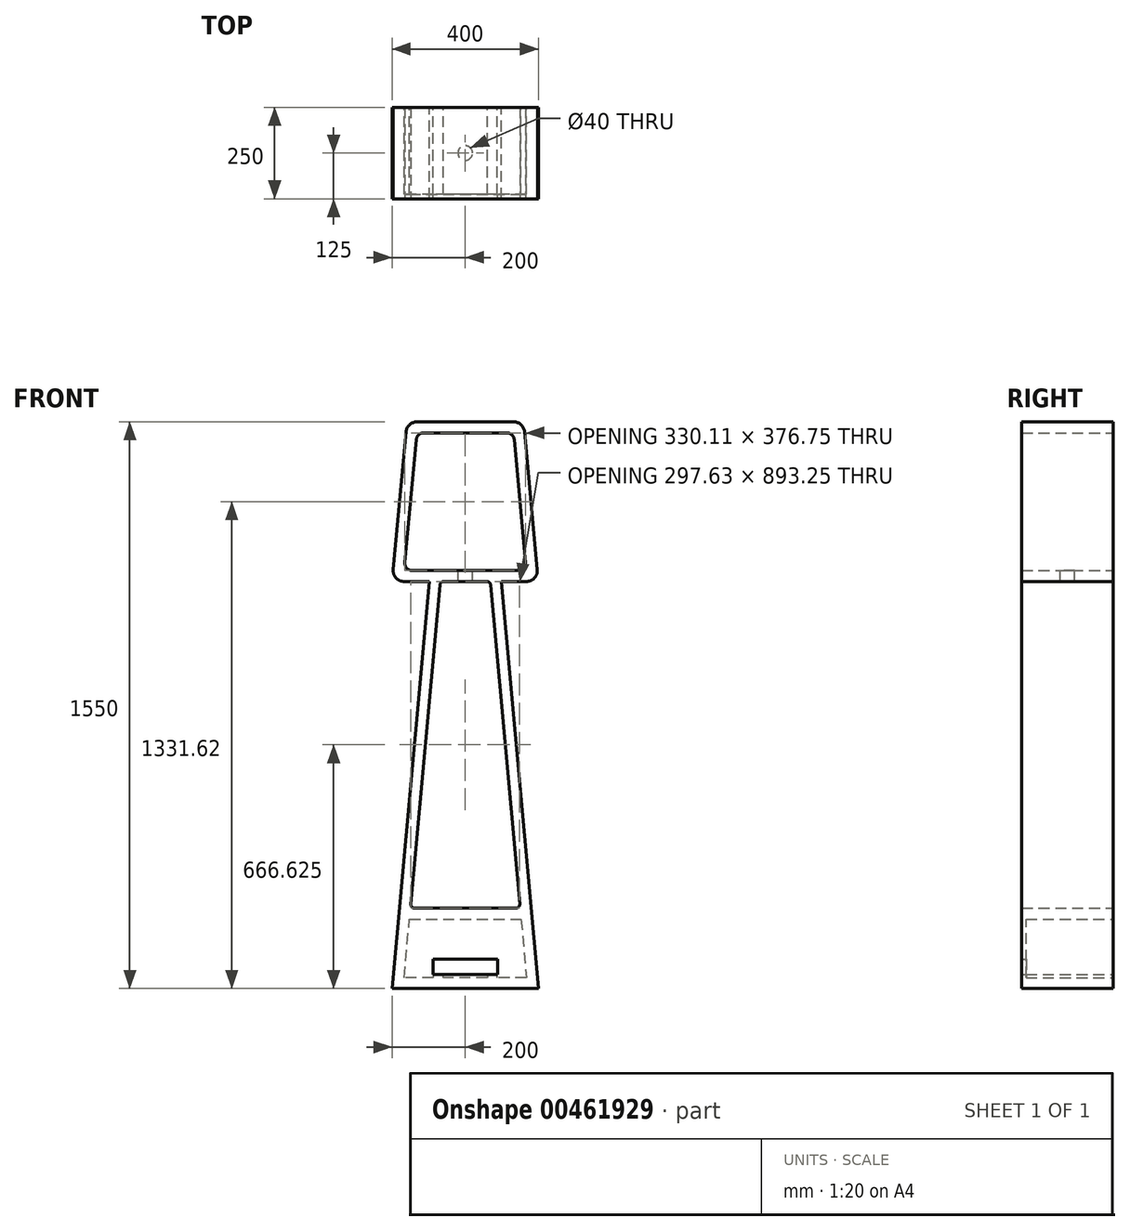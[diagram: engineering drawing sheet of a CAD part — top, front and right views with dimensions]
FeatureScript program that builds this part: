
annotation { "Feature Type Name" : "Feature", "Feature Type Description" : "" }
export const myFeature = defineFeature(function(context is Context, id is Id, definition is map)
    precondition{}
    {
        {
            var Q0;
            Q0=qCreatedBy(makeId("Front.planeOp"),FACE);
            var sketch = newSketch(context, id + "F0", { "sketchPlane" : qUnion([Q0])});
            skLineSegment(sketch, "E0", {"start": v(98.47, 1113.25) * mm, "end": v(200, 1113.25) * mm});
            skLineSegment(sketch, "E1", {"start": v(200, 1113.25) * mm, "end": v(159.42, 1550) * mm});
            skLineSegment(sketch, "E2.MirrorCS", {"start": v(-200, 1113.25) * mm, "end": v(-159.42, 1550) * mm});
            skLineSegment(sketch, "E3.MirrorCS", {"start": v(-98.47, 1113.25) * mm, "end": v(-200, 1113.25) * mm});
            skLineSegment(sketch, "E4", {"start": v(-159.42, 1550) * mm, "end": v(159.42, 1550) * mm});
            skLineSegment(sketch, "E5", {"start": v(200, 0) * mm, "end": v(-200, 0) * mm});
            skLineSegment(sketch, "E6", {"start": v(-132.08, 1520) * mm, "end": v(-167.08, 1143.25) * mm});
            skLineSegment(sketch, "E7", {"start": v(-167.08, 1143.25) * mm, "end": v(167.08, 1143.25) * mm});
            skLineSegment(sketch, "E8", {"start": v(167.08, 1143.25) * mm, "end": v(132.08, 1520) * mm});
            skLineSegment(sketch, "E9", {"start": v(132.08, 1520) * mm, "end": v(-132.08, 1520) * mm});
            skLineSegment(sketch, "E10", {"start": v(-98.47, 1113.25) * mm, "end": v(-200, 0) * mm});
            skLineSegment(sketch, "E11", {"start": v(98.47, 1113.25) * mm, "end": v(200, 0) * mm});
            skLineSegment(sketch, "E12", {"start": v(-68.35, 1113.25) * mm, "end": v(68.35, 1113.25) * mm});
            skLineSegment(sketch, "E13", {"start": v(68.35, 1113.25) * mm, "end": v(149.81, 220) * mm});
            skLineSegment(sketch, "E14", {"start": v(149.81, 220) * mm, "end": v(-149.81, 220) * mm});
            skLineSegment(sketch, "E15", {"start": v(-149.81, 220) * mm, "end": v(-68.35, 1113.25) * mm});
            skSolve(sketch);
        }
        {
            var Q0;
            Q0=makeQuery(id+"F0.imprint","IMPRINT",FACE,{"disambiguationData":[TD([[makeQuery(id+"F0.imprint","IMPRINT",EDGE,{"derivedFrom":sQuery(id+"F0.wireOp",EDGE,"E0")}),1.0]])]});
            extrude(context, id + "F1", {"entities" : qUnion([Q0]), "depth" : 250 * mm, "offsetDistance" : 25 * mm});
        }
        {
            var Q0;
            Q0=makeQuery(id+"F1.opExtrude","CAP_FACE",FACE,{"disambiguationData":[OSD([sQuery(id+"F0.wireOp",EDGE,"E0"),sQuery(id+"F0.wireOp",EDGE,"E1"),sQuery(id+"F0.wireOp",EDGE,"E2.MirrorCS"),sQuery(id+"F0.wireOp",EDGE,"E3.MirrorCS"),sQuery(id+"F0.wireOp",EDGE,"E4"),sQuery(id+"F0.wireOp",EDGE,"E5"),sQuery(id+"F0.wireOp",EDGE,"E6"),sQuery(id+"F0.wireOp",EDGE,"E7"),sQuery(id+"F0.wireOp",EDGE,"E8"),sQuery(id+"F0.wireOp",EDGE,"E9"),sQuery(id+"F0.wireOp",EDGE,"E10"),sQuery(id+"F0.wireOp",EDGE,"E11"),sQuery(id+"F0.wireOp",EDGE,"E12"),sQuery(id+"F0.wireOp",EDGE,"E13"),sQuery(id+"F0.wireOp",EDGE,"E14"),sQuery(id+"F0.wireOp",EDGE,"E15")])],"isStart":true});
            var sketch = newSketch(context, id + "F2", { "sketchPlane" : qUnion([Q0])});
            skLineSegment(sketch, "E16", {"start": v(-152.55, 190) * mm, "end": v(-167.14, 30) * mm});
            skLineSegment(sketch, "E17", {"start": v(167.14, 30) * mm, "end": v(152.55, 190) * mm});
            skLineSegment(sketch, "E18", {"start": v(152.55, 190) * mm, "end": v(-152.55, 190) * mm});
            skLineSegment(sketch, "E19", {"start": v(-167.14, 30) * mm, "end": v(-87.5, 30) * mm});
            skLineSegment(sketch, "E20", {"start": v(-87.5, 30) * mm, "end": v(-87.5, 38) * mm});
            skLineSegment(sketch, "E21", {"start": v(-87.5, 38) * mm, "end": v(-60, 38) * mm});
            skLineSegment(sketch, "E22", {"start": v(-60, 38) * mm, "end": v(-60, 30) * mm});
            skLineSegment(sketch, "E23", {"start": v(-60, 30) * mm, "end": v(60, 30) * mm});
            skLineSegment(sketch, "E24", {"start": v(60, 30) * mm, "end": v(60, 38) * mm});
            skLineSegment(sketch, "E25", {"start": v(60, 38) * mm, "end": v(87.5, 38) * mm});
            skLineSegment(sketch, "E26", {"start": v(87.5, 38) * mm, "end": v(87.5, 30) * mm});
            skLineSegment(sketch, "E27", {"start": v(87.5, 30) * mm, "end": v(167.14, 30) * mm});
            skSolve(sketch);
        }
        {
            var Q0;
            Q0=makeQuery(id+"F2.imprint","IMPRINT",FACE,{"disambiguationData":[TD([[makeQuery(id+"F2.imprint","IMPRINT",EDGE,{"derivedFrom":sQuery(id+"F2.wireOp",EDGE,"E16")}),1.0]])]});
            extrude(context, id + "F3", {"entities" : qUnion([Q0]), "operationType" : NewBodyOperationType.REMOVE, "oppositeDirection" : true, "depth" : 238 * mm, "offsetDistance" : 25 * mm});
        }
        {
            var Q0;
            Q0=makeQuery(id+"F3.boolean.opBoolean","COPY",FACE,{"derivedFrom":makeQuery(id+"F3.opExtrude","CAP_FACE",FACE,{"disambiguationData":[OSD([sQuery(id+"F2.wireOp",EDGE,"E16"),sQuery(id+"F2.wireOp",EDGE,"E17"),sQuery(id+"F2.wireOp",EDGE,"E18"),sQuery(id+"F2.wireOp",EDGE,"E19"),sQuery(id+"F2.wireOp",EDGE,"E20"),sQuery(id+"F2.wireOp",EDGE,"E21"),sQuery(id+"F2.wireOp",EDGE,"E22"),sQuery(id+"F2.wireOp",EDGE,"E23"),sQuery(id+"F2.wireOp",EDGE,"E24"),sQuery(id+"F2.wireOp",EDGE,"E25"),sQuery(id+"F2.wireOp",EDGE,"E26"),sQuery(id+"F2.wireOp",EDGE,"E27")])],"isStart":false})});
            var sketch = newSketch(context, id + "F4", { "sketchPlane" : qUnion([Q0])});
            skLineSegment(sketch, "E28.bottom", {"start": v(-88, 81) * mm, "end": v(88, 81) * mm});
            skLineSegment(sketch, "E28.top", {"start": v(-88, 38) * mm, "end": v(88, 38) * mm});
            skLineSegment(sketch, "E28.left", {"start": v(-88, 81) * mm, "end": v(-88, 38) * mm});
            skLineSegment(sketch, "E28.right", {"start": v(88, 81) * mm, "end": v(88, 38) * mm});
            skSolve(sketch);
        }
        {
            var Q0;
            Q0 = qSketchRegion(id + "F4", true);
            extrude(context, id + "F5", {"entities" : qUnion([Q0]), "operationType" : NewBodyOperationType.REMOVE, "endBound" : BoundingType.THROUGH_ALL, "oppositeDirection" : true, "depth" : 25 * mm, "offsetDistance" : 25 * mm});
        }
        {
            var Q0;
            Q0=makeQuery(id+"F1.opExtrude","SWEPT_EDGE",EDGE,{"disambiguationData":[OSD([sQuery(id+"F0.wireOp",EDGE,"E14"),sQuery(id+"F0.wireOp",EDGE,"E15")])]});
            var Q1;
            Q1=makeQuery(id+"F1.opExtrude","SWEPT_EDGE",EDGE,{"disambiguationData":[OSD([sQuery(id+"F0.wireOp",EDGE,"E13"),sQuery(id+"F0.wireOp",EDGE,"E14")])]});
            var Q2;
            Q2=makeQuery(id+"F1.opExtrude","SWEPT_EDGE",EDGE,{"disambiguationData":[OSD([sQuery(id+"F0.wireOp",EDGE,"E12"),sQuery(id+"F0.wireOp",EDGE,"E15")])]});
            var Q3;
            Q3=makeQuery(id+"F1.opExtrude","SWEPT_EDGE",EDGE,{"disambiguationData":[OSD([sQuery(id+"F0.wireOp",EDGE,"E12"),sQuery(id+"F0.wireOp",EDGE,"E13")])]});
            fillet(context, id + "F6", {"entities" : qUnion([Q0, Q1, Q2, Q3]), "radius" : 10 * mm, "tangentPropagation" : true, "allowEdgeOverflow" : false});
        }
        {
            var Q0;
            Q0=makeQuery(id+"F1.opExtrude","SWEPT_EDGE",EDGE,{"disambiguationData":[OSD([sQuery(id+"F0.wireOp",EDGE,"E0"),sQuery(id+"F0.wireOp",EDGE,"E1")])]});
            var Q1;
            Q1=makeQuery(id+"F1.opExtrude","SWEPT_EDGE",EDGE,{"disambiguationData":[OSD([sQuery(id+"F0.wireOp",EDGE,"E2.MirrorCS"),sQuery(id+"F0.wireOp",EDGE,"E3.MirrorCS")])]});
            var Q2;
            Q2=makeQuery(id+"F1.opExtrude","SWEPT_EDGE",EDGE,{"disambiguationData":[OSD([sQuery(id+"F0.wireOp",EDGE,"E2.MirrorCS"),sQuery(id+"F0.wireOp",EDGE,"E4")])]});
            var Q3;
            Q3=makeQuery(id+"F1.opExtrude","SWEPT_EDGE",EDGE,{"disambiguationData":[OSD([sQuery(id+"F0.wireOp",EDGE,"E1"),sQuery(id+"F0.wireOp",EDGE,"E4")])]});
            fillet(context, id + "F7", {"entities" : qUnion([Q0, Q1, Q2, Q3]), "radius" : 30 * mm, "tangentPropagation" : true, "allowEdgeOverflow" : false});
        }
        {
            var Q0;
            Q0=makeQuery(id+"F1.opExtrude","SWEPT_EDGE",EDGE,{"disambiguationData":[OSD([sQuery(id+"F0.wireOp",EDGE,"E6"),sQuery(id+"F0.wireOp",EDGE,"E7")])]});
            var Q1;
            Q1=makeQuery(id+"F1.opExtrude","SWEPT_EDGE",EDGE,{"disambiguationData":[OSD([sQuery(id+"F0.wireOp",EDGE,"E6"),sQuery(id+"F0.wireOp",EDGE,"E9")])]});
            var Q2;
            Q2=makeQuery(id+"F1.opExtrude","SWEPT_EDGE",EDGE,{"disambiguationData":[OSD([sQuery(id+"F0.wireOp",EDGE,"E8"),sQuery(id+"F0.wireOp",EDGE,"E9")])]});
            var Q3;
            Q3=makeQuery(id+"F1.opExtrude","SWEPT_EDGE",EDGE,{"disambiguationData":[OSD([sQuery(id+"F0.wireOp",EDGE,"E7"),sQuery(id+"F0.wireOp",EDGE,"E8")])]});
            fillet(context, id + "F8", {"entities" : qUnion([Q0, Q1, Q2, Q3]), "radius" : 20 * mm, "tangentPropagation" : true, "allowEdgeOverflow" : false});
        }
        {
            var Q0;
            Q0=makeQuery(id+"F1.opExtrude","SWEPT_FACE",FACE,{"disambiguationData":[OSD([sQuery(id+"F0.wireOp",EDGE,"E7")])]});
            var sketch = newSketch(context, id + "F9", { "sketchPlane" : qUnion([Q0])});
            skLineSegment(sketch, "E29", {"start": v(-145.14, 0) * mm, "end": v(145.14, -250) * mm, "construction": true});
            skLineSegment(sketch, "E30", {"start": v(-145.14, -250) * mm, "end": v(145.14, 0) * mm, "construction": true});
            skCircle(sketch, "E31", {"center": v(0, -125) * mm, "radius": 20 * mm});
            skSolve(sketch);
        }
        {
            var Q0;
            Q0 = qSketchRegion(id + "F9", true);
            extrude(context, id + "F10", {"entities" : qUnion([Q0]), "operationType" : NewBodyOperationType.REMOVE, "endBound" : BoundingType.UP_TO_NEXT, "oppositeDirection" : true, "depth" : 25 * mm, "offsetDistance" : 25 * mm});
        }
    });
